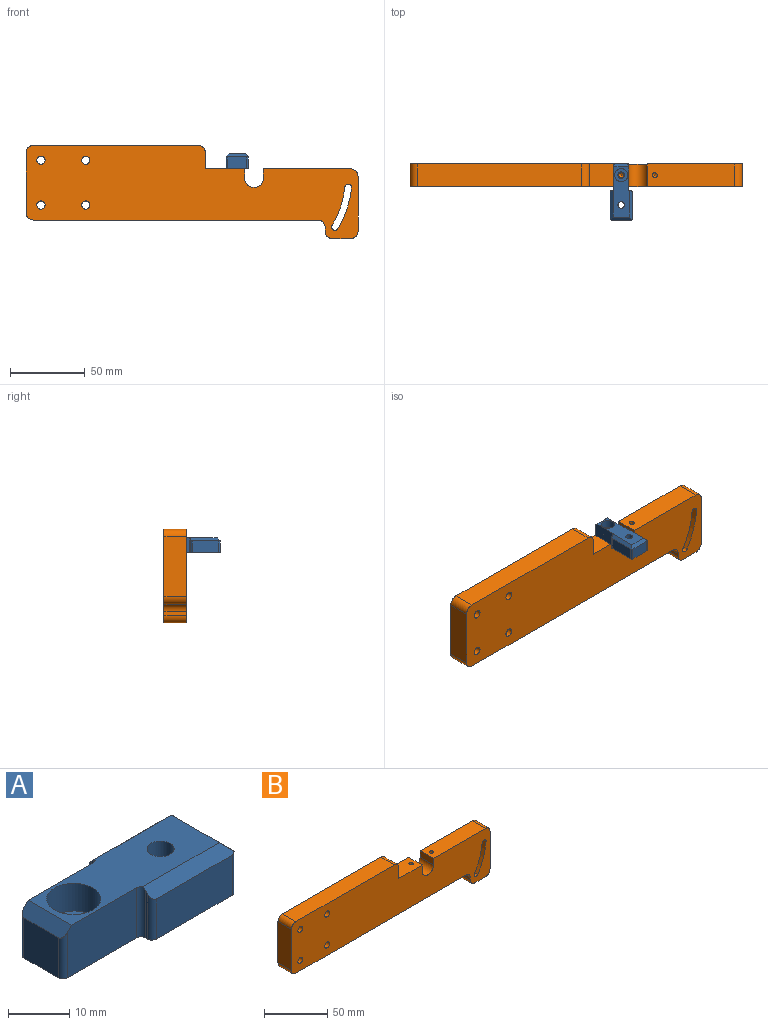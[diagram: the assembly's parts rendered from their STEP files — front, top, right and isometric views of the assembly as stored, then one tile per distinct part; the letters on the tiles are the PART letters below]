
ASSEMBLY  parts=2 mates=1
PART A: 26 faces, bbox 37.5x15x10 mm
  f0: plane 37.5x15mm, normal (0,0,-1), area 441.2mm2, adj f2,f3,f4,f5,f6,f12,f13,f14
  f1: plane 33.5x11mm, normal (0,0,1), area 276.9mm2, adj f6,f7,f8,f9,f10,f14,f17,f19
  f2: cylinder r=2.2mm len=4.5mm, axis (0,0,1), area 62.2mm2, adj f0,f11
  f3: plane 17.5x8mm, normal (0,1,0), area 140mm2, adj f0,f9,f13,f23
  f4: plane 17.5x8mm, normal (0,-1,0), area 140mm2, adj f0,f8,f12,f16
  f5: plane 13x8mm, normal (1,0,0), area 104mm2, adj f0,f7,f12,f13
  f6: cylinder r=2.2mm len=10mm, axis (0,0,1), area 138.2mm2, adj f0,f1
  f7: plane 14.41x2mm, normal (0.71,0,0.71), area 36.5mm2, adj f1,f5,f8,f9,f12,f13
  f8: plane 19.36x2.02mm, normal (0,-0.71,0.71), area 51.9mm2, adj f1,f4,f7,f12,f15,f16,f17
  f9: plane 19.36x2.02mm, normal (0,0.71,0.71), area 51.9mm2, adj f1,f3,f7,f13,f22,f23,f24
  f10: cylinder r=4.4mm len=8.8mm, axis (0,0,1), area 152.1mm2, adj f1,f11
  f11: plane 8.8x8.8mm, normal (0,0,1), area 45.6mm2, adj f2,f10
  f12: cylinder r=1mm len=8.29mm, axis (0,0,1), area 12.7mm2, adj f0,f4,f5,f7,f8
  f13: cylinder r=1mm len=8.29mm, axis (0,0,-1), area 12.7mm2, adj f0,f3,f5,f7,f9
  f14: plane 16x10mm, normal (0,-1,0), area 159.5mm2, adj f0,f1,f17,f19,f20
  f15: plane 9.5x0.5mm, normal (-1,0,0), area 4.6mm2, adj f0,f8,f16,f17
  f16: cylinder r=1mm len=9mm, axis (0,0,-1), area 13.1mm2, adj f0,f4,f8,f15
  f17: cylinder r=1mm len=10mm, axis (0,0,1), area 15.6mm2, adj f0,f1,f8,f14,f15
  f18: plane 8x8mm, normal (-1,0,0), area 64mm2, adj f0,f19,f20,f25
  f19: plane 10x2mm, normal (-0.71,0,0.71), area 27.7mm2, adj f1,f14,f18,f20,f21,f25
  f20: cylinder r=1mm len=9mm, axis (0,0,-1), area 13.1mm2, adj f0,f14,f18,f19
  f21: plane 16x10mm, normal (0,1,0), area 159.5mm2, adj f0,f1,f19,f24,f25
  f22: plane 9.5x0.5mm, normal (-1,0,0), area 4.6mm2, adj f0,f9,f23,f24
  f23: cylinder r=1mm len=9mm, axis (0,0,1), area 13.1mm2, adj f0,f3,f9,f22
  f24: cylinder r=1mm len=10mm, axis (0,0,1), area 15.6mm2, adj f0,f1,f9,f21,f22
  f25: cylinder r=1mm len=9mm, axis (0,0,-1), area 13.1mm2, adj f0,f18,f19,f21
PART B: 33 faces, bbox 222x15x62.5 mm
  f0: plane 222x62.5mm, normal (0,-1,0), area 9365mm2, adj f2,f3,f4,f5,f6,f7,f8,f9
  f1: plane 222x62.5mm, normal (0,1,0), area 9365mm2, adj f2,f3,f4,f5,f6,f7,f8,f9
  f2: plane 190x15mm, normal (0,0,-1), area 2850mm2, adj f0,f1,f26,f32
  f3: plane 58.25x15mm, normal (0,0,1), area 865.2mm2, adj f0,f1,f14,f19,f29
  f4: plane 15x10.75mm, normal (1,0,0), area 161.2mm2, adj f0,f1,f13,f30
  f5: plane 110x15mm, normal (0,0,1), area 1650mm2, adj f0,f1,f30,f31
  f6: plane 40x15mm, normal (-1,0,0), area 600mm2, adj f0,f1,f31,f32
  f7: cylinder r=2.75mm len=15mm, axis (0,-1,0), area 259.2mm2, adj f0,f1
  f8: cylinder r=2.75mm len=15mm, axis (0,-1,0), area 259.2mm2, adj f0,f1
  f9: cylinder r=2.75mm len=15mm, axis (0,-1,0), area 259.2mm2, adj f0,f1
  f10: cylinder r=2.75mm len=15mm, axis (0,-1,0), area 259.2mm2, adj f0,f1
  f11: cylinder r=6.25mm len=15mm, axis (0,-1,0), area 294.5mm2, adj f0,f1,f12,f14
  f12: plane 15x6.25mm, normal (1,0,0), area 93.7mm2, adj f0,f1,f11,f13
  f13: plane 26.25x15mm, normal (0,0,1), area 385.2mm2, adj f0,f1,f4,f12,f17
  f14: plane 15x6.25mm, normal (-1,0,0), area 93.7mm2, adj f0,f1,f3,f11
  f15: plane 36.75x15mm, normal (1,0,0), area 551.3mm2, adj f0,f1,f27,f29
  f16: cone r=0mm half-angle=59deg, axis (0,0,1), area 10mm2, adj f17
  f17: cylinder r=1.65mm len=15mm, axis (0,0,1), area 155.5mm2, adj f13,f16
  f18: cone r=0mm half-angle=59deg, axis (0,0,1), area 10mm2, adj f19
  f19: cylinder r=1.65mm len=15mm, axis (0,0,1), area 155.5mm2, adj f3,f18
  f20: plane 15x2.5mm, normal (-1,0,0), area 37.5mm2, adj f0,f1,f26,f28
  f21: plane 15x12mm, normal (0,0,-1), area 180mm2, adj f0,f1,f27,f28
  f22: cylinder r=61mm len=25.46mm, axis (0,1,0), area 405.9mm2, adj f0,f1,f23,f25
  f23: cylinder r=2.25mm len=15mm, axis (0,1,0), area 106mm2, adj f0,f1,f22,f24
  f24: cylinder r=65.5mm len=27.34mm, axis (0,1,0), area 435.8mm2, adj f0,f1,f23,f25
  f25: cylinder r=2.25mm len=15mm, axis (0,1,0), area 106mm2, adj f0,f1,f22,f24
  f26: cylinder r=5mm len=15mm, axis (0,1,0), area 117.8mm2, adj f0,f1,f2,f20
  f27: cylinder r=5mm len=15mm, axis (0,-1,0), area 117.8mm2, adj f0,f1,f15,f21
  f28: cylinder r=5mm len=15mm, axis (0,-1,0), area 117.8mm2, adj f0,f1,f20,f21
  f29: cylinder r=5mm len=15mm, axis (0,-1,0), area 117.8mm2, adj f0,f1,f3,f15
  f30: cylinder r=5mm len=15mm, axis (0,1,0), area 117.8mm2, adj f0,f1,f4,f5
  f31: cylinder r=5mm len=15mm, axis (0,-1,0), area 117.8mm2, adj f0,f1,f5,f6
  f32: cylinder r=5mm len=15mm, axis (0,1,0), area 117.8mm2, adj f0,f1,f2,f6
PLACE A rot(axis=(0,0,-1),90deg) t=(-9.23,-41.02,18.77)mm
PLACE B t=(-30.48,-23.52,9.52)mm
MATE cylindrical A.f2 <-> B.f16  axis (0,0,-1) through (-9.23,-31.02,18.77)mm
